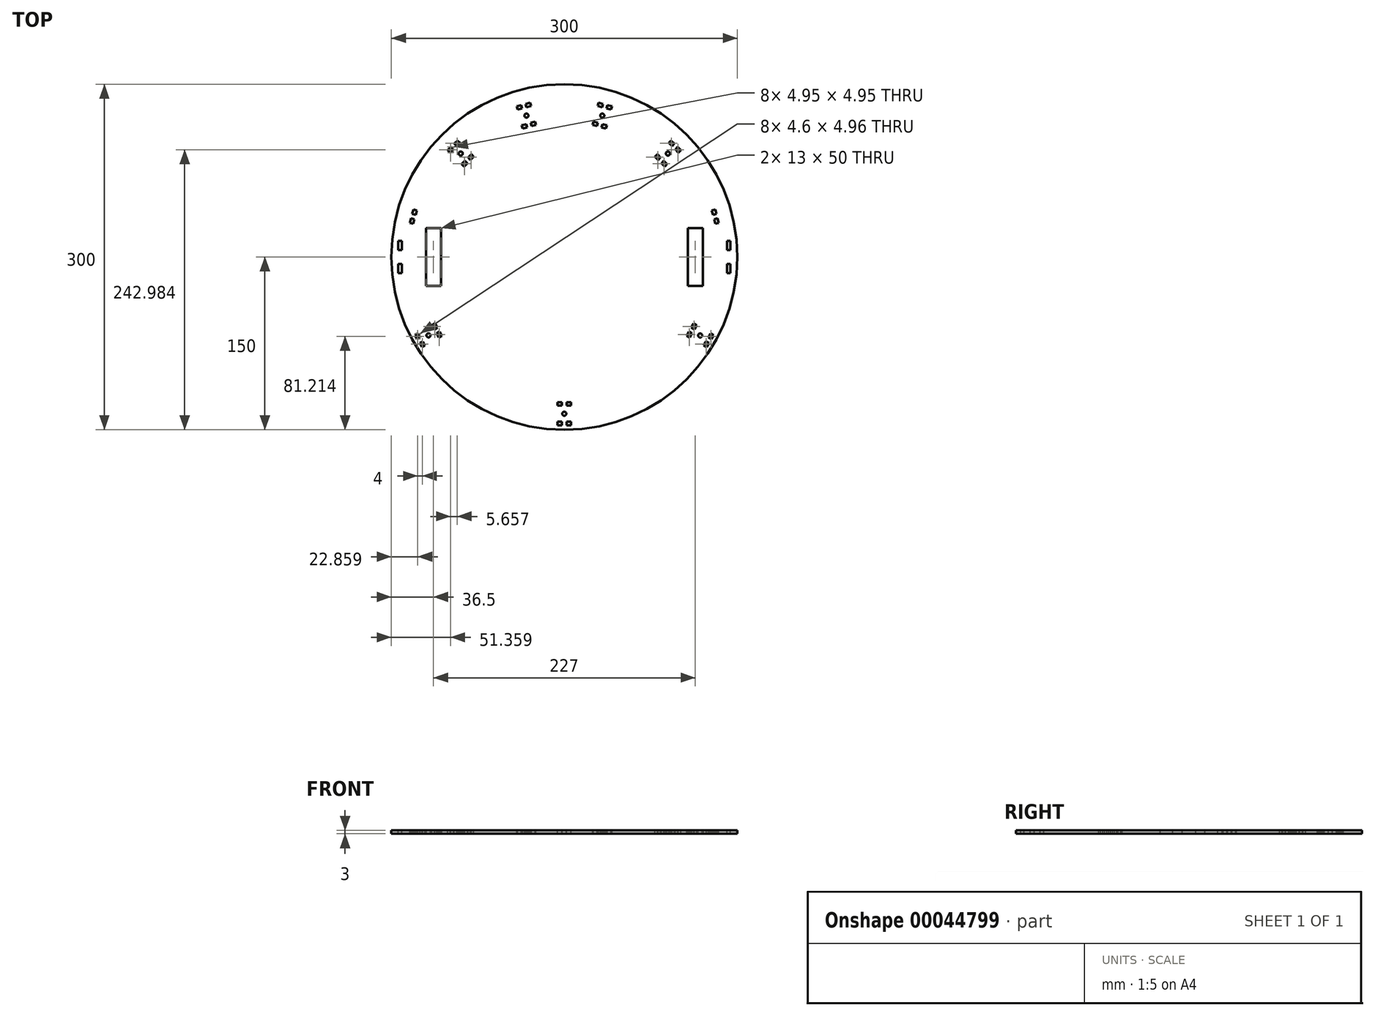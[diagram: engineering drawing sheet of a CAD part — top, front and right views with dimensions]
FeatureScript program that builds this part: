
annotation { "Feature Type Name" : "Feature", "Feature Type Description" : "" }
export const myFeature = defineFeature(function(context is Context, id is Id, definition is map)
    precondition{}
    {
        {
            var Q0;
            Q0=qCreatedBy(makeId("Top.planeOp"),FACE);
            var sketch = newSketch(context, id + "F0", { "sketchPlane" : qUnion([Q0])});
            skCircle(sketch, "E0", {"center": v(0, 0) * mm, "radius": 150 * mm});
            skLineSegment(sketch, "E1", {"start": v(0, 150) * mm, "end": v(0, -150) * mm, "construction": true});
            skLineSegment(sketch, "E2.bottom", {"start": v(-120, 25) * mm, "end": v(-107, 25) * mm});
            skLineSegment(sketch, "E2.top", {"start": v(-120, -25) * mm, "end": v(-107, -25) * mm});
            skLineSegment(sketch, "E2.left", {"start": v(-120, 25) * mm, "end": v(-120, -25) * mm});
            skLineSegment(sketch, "E2.right", {"start": v(-107, 25) * mm, "end": v(-107, -25) * mm});
            skLineSegment(sketch, "E3.bottom", {"start": v(-144, -6) * mm, "end": v(-141, -6) * mm});
            skLineSegment(sketch, "E3.top", {"start": v(-144, -14) * mm, "end": v(-141, -14) * mm});
            skLineSegment(sketch, "E3.left", {"start": v(-144, -6) * mm, "end": v(-144, -14) * mm});
            skLineSegment(sketch, "E3.right", {"start": v(-141, -6) * mm, "end": v(-141, -14) * mm});
            skLineSegment(sketch, "E4", {"start": v(150, 0) * mm, "end": v(-150, 0) * mm, "construction": true});
            skPoint(sketch, "E5", {"position": v(-107, 0) * mm});
            skLineSegment(sketch, "E6.MirrorCS", {"start": v(-144, 14) * mm, "end": v(-141, 14) * mm});
            skLineSegment(sketch, "E7.MirrorCS", {"start": v(-141, 6) * mm, "end": v(-141, 14) * mm});
            skLineSegment(sketch, "E8.MirrorCS", {"start": v(-144, 6) * mm, "end": v(-144, 14) * mm});
            skLineSegment(sketch, "E9.MirrorCS", {"start": v(-144, 6) * mm, "end": v(-141, 6) * mm});
            skLineSegment(sketch, "E10.MirrorCS", {"start": v(144, 6) * mm, "end": v(141, 6) * mm});
            skLineSegment(sketch, "E11.MirrorCS", {"start": v(144, 14) * mm, "end": v(141, 14) * mm});
            skLineSegment(sketch, "E12.MirrorCS", {"start": v(144, -6) * mm, "end": v(141, -6) * mm});
            skLineSegment(sketch, "E13.MirrorCS", {"start": v(144, -14) * mm, "end": v(141, -14) * mm});
            skLineSegment(sketch, "E14.MirrorCS", {"start": v(144, -6) * mm, "end": v(144, -14) * mm});
            skLineSegment(sketch, "E15.MirrorCS", {"start": v(141, -6) * mm, "end": v(141, -14) * mm});
            skLineSegment(sketch, "E16.MirrorCS", {"start": v(144, 6) * mm, "end": v(144, 14) * mm});
            skLineSegment(sketch, "E17.MirrorCS", {"start": v(107, 25) * mm, "end": v(107, -25) * mm});
            skLineSegment(sketch, "E18.MirrorCS", {"start": v(120, 25) * mm, "end": v(120, -25) * mm});
            skLineSegment(sketch, "E19.MirrorCS", {"start": v(120, -25) * mm, "end": v(107, -25) * mm});
            skLineSegment(sketch, "E20.MirrorCS", {"start": v(120, 25) * mm, "end": v(107, 25) * mm});
            skPoint(sketch, "E21.MirrorP", {"position": v(107, 0) * mm});
            skLineSegment(sketch, "E22.MirrorCS", {"start": v(141, 6) * mm, "end": v(141, 14) * mm});
            skSolve(sketch);
        }
        {
            var Q0;
            Q0=makeQuery(id+"F0.imprint","IMPRINT",FACE,{"disambiguationData":[TD([[makeQuery(id+"F0.imprint","IMPRINT",EDGE,{"derivedFrom":sQuery(id+"F0.wireOp",EDGE,"E0")}),1.0]])]});
            extrude(context, id + "F1", {"entities" : qUnion([Q0]), "oppositeDirection" : true, "depth" : 3 * mm});
        }
        {
            var Q0;
            Q0=makeQuery(id+"F1.opExtrude","CAP_FACE",FACE,{"disambiguationData":[OSD([sQuery(id+"F0.wireOp",EDGE,"E0"),sQuery(id+"F0.wireOp",EDGE,"E2.bottom"),sQuery(id+"F0.wireOp",EDGE,"E2.top"),sQuery(id+"F0.wireOp",EDGE,"E2.left"),sQuery(id+"F0.wireOp",EDGE,"E2.right"),sQuery(id+"F0.wireOp",EDGE,"E3.bottom"),sQuery(id+"F0.wireOp",EDGE,"E3.top"),sQuery(id+"F0.wireOp",EDGE,"E3.left"),sQuery(id+"F0.wireOp",EDGE,"E3.right"),sQuery(id+"F0.wireOp",EDGE,"cbf36644-4c9d-44f4-99aa-729f08500aa81.MirrorCS"),sQuery(id+"F0.wireOp",EDGE,"cbf36644-4c9d-44f4-99aa-729f08500aa82.MirrorCS"),sQuery(id+"F0.wireOp",EDGE,"cbf36644-4c9d-44f4-99aa-729f08500aa83.MirrorCS"),sQuery(id+"F0.wireOp",EDGE,"cbf36644-4c9d-44f4-99aa-729f08500aa84.MirrorCS"),sQuery(id+"F0.wireOp",EDGE,"868d1104-2d39-4a06-ab7a-803dcc4c7a7c1.MirrorCS"),sQuery(id+"F0.wireOp",EDGE,"868d1104-2d39-4a06-ab7a-803dcc4c7a7c2.MirrorCS"),sQuery(id+"F0.wireOp",EDGE,"868d1104-2d39-4a06-ab7a-803dcc4c7a7c3.MirrorCS"),sQuery(id+"F0.wireOp",EDGE,"868d1104-2d39-4a06-ab7a-803dcc4c7a7c4.MirrorCS")])],"isStart":true});
            var sketch = newSketch(context, id + "F2", { "sketchPlane" : qUnion([Q0])});
            skCircle(sketch, "E23.0", {"center": v(0, 0) * mm, "radius": 150 * mm, "construction": true});
            skLineSegment(sketch, "E24.1", {"start": v(0, 150) * mm, "end": v(0, -150) * mm, "construction": true});
            skLineSegment(sketch, "E25.2", {"start": v(150, 0) * mm, "end": v(-150, 0) * mm, "construction": true});
            skCircle(sketch, "E26.0", {"center": v(0, 0) * mm, "radius": 151 * mm, "construction": true});
            skCircle(sketch, "E27.0", {"center": v(0, 0) * mm, "radius": 154 * mm, "construction": true});
            skLineSegment(sketch, "E28", {"start": v(0, 150) * mm, "end": v(0, 151) * mm, "construction": true});
            skLineSegment(sketch, "E29", {"start": v(0, 151) * mm, "end": v(0, 154) * mm, "construction": true});
            skLineSegment(sketch, "E30", {"start": v(0, 0) * mm, "end": v(-75, 129.9) * mm, "construction": true});
            skLineSegment(sketch, "E31", {"start": v(-75, 129.9) * mm, "end": v(-75.5, 130.77) * mm, "construction": true});
            skLineSegment(sketch, "E32", {"start": v(-75.5, 130.77) * mm, "end": v(-77, 133.37) * mm, "construction": true});
            skLineSegment(sketch, "E33", {"start": v(0, 0) * mm, "end": v(-150, 0) * mm, "construction": true});
            skLineSegment(sketch, "E34", {"start": v(-150, 0) * mm, "end": v(-151, 0) * mm, "construction": true});
            skLineSegment(sketch, "E35", {"start": v(-151, 0) * mm, "end": v(-154, 0) * mm, "construction": true});
            skLineSegment(sketch, "E36", {"start": v(0, 0) * mm, "end": v(-38.82, 144.89) * mm, "construction": true});
            skLineSegment(sketch, "E37", {"start": v(-38.82, 144.89) * mm, "end": v(-39.08, 145.85) * mm, "construction": true});
            skLineSegment(sketch, "E38", {"start": v(-39.08, 145.85) * mm, "end": v(-39.86, 148.75) * mm, "construction": true});
            skLineSegment(sketch, "E39", {"start": v(-41.25, 130.78) * mm, "end": v(-37.4, 131.81) * mm});
            skLineSegment(sketch, "E40", {"start": v(-37.4, 131.81) * mm, "end": v(-36.61, 128.92) * mm});
            skLineSegment(sketch, "E41", {"start": v(-36.61, 128.92) * mm, "end": v(-40.48, 127.88) * mm});
            skLineSegment(sketch, "E42", {"start": v(-40.48, 127.88) * mm, "end": v(-41.25, 130.78) * mm});
            skLineSegment(sketch, "E43", {"start": v(-33, 115.4) * mm, "end": v(-36.85, 114.36) * mm});
            skLineSegment(sketch, "E44", {"start": v(-36.85, 114.36) * mm, "end": v(-36.08, 111.46) * mm});
            skLineSegment(sketch, "E45", {"start": v(-36.08, 111.46) * mm, "end": v(-32.21, 112.5) * mm});
            skLineSegment(sketch, "E46", {"start": v(-33, 115.4) * mm, "end": v(-32.21, 112.5) * mm});
            skCircle(sketch, "E47", {"center": v(-32.87, 122.67) * mm, "radius": 1.75 * mm});
            skLineSegment(sketch, "E48.MirrorCS", {"start": v(-29.66, 133.88) * mm, "end": v(-33.53, 132.85) * mm});
            skLineSegment(sketch, "E49.MirrorCS", {"start": v(-33.53, 132.85) * mm, "end": v(-32.75, 129.95) * mm});
            skLineSegment(sketch, "E50.MirrorCS", {"start": v(-32.75, 129.95) * mm, "end": v(-28.89, 130.99) * mm});
            skLineSegment(sketch, "E51.MirrorCS", {"start": v(-29.13, 116.43) * mm, "end": v(-25.26, 117.46) * mm});
            skLineSegment(sketch, "E52.MirrorCS", {"start": v(-29.13, 116.43) * mm, "end": v(-28.35, 113.53) * mm});
            skLineSegment(sketch, "E53.MirrorCS", {"start": v(-24.49, 114.57) * mm, "end": v(-28.35, 113.53) * mm});
            skLineSegment(sketch, "E54.MirrorCS", {"start": v(-25.26, 117.46) * mm, "end": v(-24.49, 114.57) * mm});
            skLineSegment(sketch, "E55.MirrorCS", {"start": v(-28.89, 130.99) * mm, "end": v(-29.66, 133.88) * mm});
            skLineSegment(sketch, "E56.anchor1", {"start": v(0, 0) * mm, "end": v(-32.87, 122.67) * mm, "construction": true});
            skLineSegment(sketch, "E57", {"start": v(0, 0) * mm, "end": v(-133.37, -77) * mm, "construction": true});
            skCircle(sketch, "E58", {"center": v(-117.78, -68) * mm, "radius": 1.75 * mm});
            skLineSegment(sketch, "E59", {"start": v(-110.72, -66.23) * mm, "end": v(-108.72, -69.7) * mm});
            skLineSegment(sketch, "E60", {"start": v(-122.84, -73.23) * mm, "end": v(-120.84, -76.7) * mm});
            skLineSegment(sketch, "E61", {"start": v(-125.44, -74.73) * mm, "end": v(-122.84, -73.23) * mm});
            skLineSegment(sketch, "E62", {"start": v(-110.72, -66.23) * mm, "end": v(-108.12, -64.73) * mm});
            skLineSegment(sketch, "E63", {"start": v(-106.12, -68.2) * mm, "end": v(-108.12, -64.73) * mm});
            skLineSegment(sketch, "E64", {"start": v(-123.44, -78.2) * mm, "end": v(-125.44, -74.73) * mm});
            skLineSegment(sketch, "E65", {"start": v(-108.72, -69.7) * mm, "end": v(-106.12, -68.2) * mm});
            skLineSegment(sketch, "E66", {"start": v(-120.84, -76.7) * mm, "end": v(-123.44, -78.2) * mm});
            skPoint(sketch, "E67", {"position": v(-130.77, -75.5) * mm});
            skLineSegment(sketch, "E68.MirrorCS", {"start": v(-112.72, -62.77) * mm, "end": v(-110.12, -61.27) * mm});
            skLineSegment(sketch, "E69.MirrorCS", {"start": v(-112.12, -57.8) * mm, "end": v(-110.12, -61.27) * mm});
            skLineSegment(sketch, "E70.MirrorCS", {"start": v(-114.72, -59.3) * mm, "end": v(-112.12, -57.8) * mm});
            skLineSegment(sketch, "E71.MirrorCS", {"start": v(-112.72, -62.77) * mm, "end": v(-114.72, -59.3) * mm});
            skLineSegment(sketch, "E72.MirrorCS", {"start": v(-124.84, -69.77) * mm, "end": v(-126.84, -66.3) * mm});
            skLineSegment(sketch, "E73.MirrorCS", {"start": v(-126.84, -66.3) * mm, "end": v(-129.44, -67.8) * mm});
            skLineSegment(sketch, "E74.MirrorCS", {"start": v(-127.44, -71.27) * mm, "end": v(-124.84, -69.77) * mm});
            skLineSegment(sketch, "E75.MirrorCS", {"start": v(-129.44, -67.8) * mm, "end": v(-127.44, -71.27) * mm});
            skLineSegment(sketch, "E76.MirrorCS", {"start": v(110.72, -66.23) * mm, "end": v(108.12, -64.73) * mm});
            skLineSegment(sketch, "E77.MirrorCS", {"start": v(110.72, -66.23) * mm, "end": v(108.72, -69.7) * mm});
            skLineSegment(sketch, "E78.MirrorCS", {"start": v(129.44, -67.8) * mm, "end": v(127.44, -71.27) * mm});
            skLineSegment(sketch, "E79.MirrorCS", {"start": v(127.44, -71.27) * mm, "end": v(124.84, -69.77) * mm});
            skLineSegment(sketch, "E80.MirrorCS", {"start": v(114.72, -59.3) * mm, "end": v(112.12, -57.8) * mm});
            skLineSegment(sketch, "E81.MirrorCS", {"start": v(112.12, -57.8) * mm, "end": v(110.12, -61.27) * mm});
            skLineSegment(sketch, "E82.MirrorCS", {"start": v(112.72, -62.77) * mm, "end": v(110.12, -61.27) * mm});
            skLineSegment(sketch, "E83.MirrorCS", {"start": v(112.72, -62.77) * mm, "end": v(114.72, -59.3) * mm});
            skLineSegment(sketch, "E84.MirrorCS", {"start": v(124.84, -69.77) * mm, "end": v(126.84, -66.3) * mm});
            skLineSegment(sketch, "E85.MirrorCS", {"start": v(126.84, -66.3) * mm, "end": v(129.44, -67.8) * mm});
            skLineSegment(sketch, "E86.MirrorCS", {"start": v(106.12, -68.2) * mm, "end": v(108.12, -64.73) * mm});
            skLineSegment(sketch, "E87.MirrorCS", {"start": v(108.72, -69.7) * mm, "end": v(106.12, -68.2) * mm});
            skCircle(sketch, "E88.MirrorC", {"center": v(117.78, -68) * mm, "radius": 1.75 * mm});
            skLineSegment(sketch, "E89.MirrorCS", {"start": v(125.44, -74.73) * mm, "end": v(122.84, -73.23) * mm});
            skLineSegment(sketch, "E90.MirrorCS", {"start": v(122.84, -73.23) * mm, "end": v(120.84, -76.7) * mm});
            skLineSegment(sketch, "E91.MirrorCS", {"start": v(123.44, -78.2) * mm, "end": v(125.44, -74.73) * mm});
            skLineSegment(sketch, "E92.MirrorCS", {"start": v(120.84, -76.7) * mm, "end": v(123.44, -78.2) * mm});
            skPoint(sketch, "E93.MirrorP", {"position": v(130.77, -75.5) * mm});
            skPoint(sketch, "E94.1.0", {"position": v(0, -151) * mm});
            skCircle(sketch, "E94.1.1", {"center": v(0, -136) * mm, "radius": 1.75 * mm});
            skPoint(sketch, "E94.1.2", {"position": v(0, -151) * mm});
            skLineSegment(sketch, "E94.1.3", {"start": v(6, -129) * mm, "end": v(6, -126) * mm});
            skLineSegment(sketch, "E94.1.4", {"start": v(-2, -129) * mm, "end": v(-2, -126) * mm});
            skLineSegment(sketch, "E94.1.5", {"start": v(6, -143) * mm, "end": v(6, -146) * mm});
            skLineSegment(sketch, "E94.1.6", {"start": v(-6, -129) * mm, "end": v(-6, -126) * mm});
            skLineSegment(sketch, "E94.1.7", {"start": v(-2, -143) * mm, "end": v(-6, -143) * mm});
            skLineSegment(sketch, "E94.1.8", {"start": v(-6, -143) * mm, "end": v(-6, -146) * mm});
            skLineSegment(sketch, "E94.1.9", {"start": v(-2, -146) * mm, "end": v(-2, -143) * mm});
            skLineSegment(sketch, "E94.1.10", {"start": v(6, -146) * mm, "end": v(2, -146) * mm});
            skLineSegment(sketch, "E94.1.11", {"start": v(2, -143) * mm, "end": v(6, -143) * mm});
            skLineSegment(sketch, "E94.1.12", {"start": v(2, -146) * mm, "end": v(2, -143) * mm});
            skLineSegment(sketch, "E94.1.13", {"start": v(-6, -146) * mm, "end": v(-2, -146) * mm});
            skLineSegment(sketch, "E94.1.14", {"start": v(2, -129) * mm, "end": v(6, -129) * mm});
            skLineSegment(sketch, "E94.1.15", {"start": v(6, -126) * mm, "end": v(2, -126) * mm});
            skLineSegment(sketch, "E94.1.16", {"start": v(2, -129) * mm, "end": v(2, -126) * mm});
            skLineSegment(sketch, "E94.1.17", {"start": v(-2, -129) * mm, "end": v(-6, -129) * mm});
            skLineSegment(sketch, "E94.1.18", {"start": v(-6, -126) * mm, "end": v(-2, -126) * mm});
            skLineSegment(sketch, "E94.anchor1", {"start": v(0, 0) * mm, "end": v(-130.77, -75.5) * mm, "construction": true});
            skLineSegment(sketch, "E94.anchor2", {"start": v(0, 0) * mm, "end": v(0, -151) * mm, "construction": true});
            skLineSegment(sketch, "E95.1.0", {"start": v(-86.97, 78.49) * mm, "end": v(-84.15, 81.32) * mm});
            skLineSegment(sketch, "E95.1.1", {"start": v(-89.1, 80.61) * mm, "end": v(-86.97, 78.49) * mm});
            skLineSegment(sketch, "E95.1.2", {"start": v(-86.27, 83.44) * mm, "end": v(-84.15, 81.32) * mm});
            skLineSegment(sketch, "E95.1.3", {"start": v(-83.44, 86.27) * mm, "end": v(-81.32, 84.15) * mm});
            skLineSegment(sketch, "E95.1.4", {"start": v(-78.49, 86.97) * mm, "end": v(-81.32, 84.15) * mm});
            skLineSegment(sketch, "E95.1.5", {"start": v(-86.27, 83.44) * mm, "end": v(-89.1, 80.61) * mm});
            skLineSegment(sketch, "E95.1.6", {"start": v(-80.61, 89.1) * mm, "end": v(-78.49, 86.97) * mm});
            skLineSegment(sketch, "E95.1.7", {"start": v(-83.44, 86.27) * mm, "end": v(-80.61, 89.1) * mm});
            skCircle(sketch, "E95.1.8", {"center": v(-89.8, 89.8) * mm, "radius": 1.75 * mm});
            skLineSegment(sketch, "E95.1.9", {"start": v(-99, 90.5) * mm, "end": v(-101.12, 92.63) * mm});
            skLineSegment(sketch, "E95.1.10", {"start": v(-96.17, 93.34) * mm, "end": v(-99, 90.5) * mm});
            skLineSegment(sketch, "E95.1.11", {"start": v(-98.29, 95.46) * mm, "end": v(-96.17, 93.34) * mm});
            skLineSegment(sketch, "E95.1.12", {"start": v(-93.34, 96.17) * mm, "end": v(-90.5, 99) * mm});
            skLineSegment(sketch, "E95.1.13", {"start": v(-101.12, 92.63) * mm, "end": v(-98.29, 95.46) * mm});
            skLineSegment(sketch, "E95.1.14", {"start": v(-95.46, 98.29) * mm, "end": v(-93.34, 96.17) * mm});
            skLineSegment(sketch, "E95.1.15", {"start": v(-90.5, 99) * mm, "end": v(-92.63, 101.12) * mm});
            skLineSegment(sketch, "E95.1.16", {"start": v(-92.63, 101.12) * mm, "end": v(-95.46, 98.29) * mm});
            skLineSegment(sketch, "E95.1.17", {"start": v(-106.07, 106.07) * mm, "end": v(-106.77, 106.77) * mm, "construction": true});
            skLineSegment(sketch, "E95.1.18", {"start": v(-106.77, 106.77) * mm, "end": v(-108.9, 108.9) * mm, "construction": true});
            skLineSegment(sketch, "E95.1.19", {"start": v(0, 0) * mm, "end": v(-106.07, 106.07) * mm, "construction": true});
            skLineSegment(sketch, "E95.anchor2", {"start": v(0, 0) * mm, "end": v(-89.8, 89.8) * mm, "construction": true});
            skLineSegment(sketch, "E96.1.0", {"start": v(-130.99, 28.89) * mm, "end": v(-133.88, 29.66) * mm});
            skLineSegment(sketch, "E96.1.1", {"start": v(-129.95, 32.75) * mm, "end": v(-130.99, 28.89) * mm});
            skLineSegment(sketch, "E96.1.2", {"start": v(-133.88, 29.66) * mm, "end": v(-132.85, 33.53) * mm});
            skLineSegment(sketch, "E96.1.3", {"start": v(-132.85, 33.53) * mm, "end": v(-129.95, 32.75) * mm});
            skLineSegment(sketch, "E96.1.4", {"start": v(-131.81, 37.4) * mm, "end": v(-128.92, 36.61) * mm});
            skLineSegment(sketch, "E96.1.5", {"start": v(-128.92, 36.61) * mm, "end": v(-127.88, 40.48) * mm});
            skLineSegment(sketch, "E96.1.6", {"start": v(-130.78, 41.25) * mm, "end": v(-131.81, 37.4) * mm});
            skLineSegment(sketch, "E96.1.7", {"start": v(-127.88, 40.48) * mm, "end": v(-130.78, 41.25) * mm});
            skLineSegment(sketch, "E96.1.8", {"start": v(0, 0) * mm, "end": v(-122.67, 32.87) * mm, "construction": true});
            skLineSegment(sketch, "E96.1.9", {"start": v(0, 0) * mm, "end": v(-144.89, 38.82) * mm, "construction": true});
            skLineSegment(sketch, "E96.1.10", {"start": v(-145.85, 39.08) * mm, "end": v(-148.75, 39.86) * mm, "construction": true});
            skLineSegment(sketch, "E96.1.11", {"start": v(-144.89, 38.82) * mm, "end": v(-145.85, 39.08) * mm, "construction": true});
            skLineSegment(sketch, "E96.anchor2", {"start": v(0, 0) * mm, "end": v(-122.67, 32.87) * mm, "construction": true});
            skLineSegment(sketch, "E97.MirrorCS", {"start": v(29.66, 133.88) * mm, "end": v(33.53, 132.85) * mm});
            skLineSegment(sketch, "E98.MirrorCS", {"start": v(28.89, 130.99) * mm, "end": v(29.66, 133.88) * mm});
            skLineSegment(sketch, "E99.MirrorCS", {"start": v(41.25, 130.78) * mm, "end": v(37.4, 131.81) * mm});
            skLineSegment(sketch, "E100.MirrorCS", {"start": v(33.53, 132.85) * mm, "end": v(32.75, 129.95) * mm});
            skLineSegment(sketch, "E101.MirrorCS", {"start": v(32.75, 129.95) * mm, "end": v(28.89, 130.99) * mm});
            skLineSegment(sketch, "E102.MirrorCS", {"start": v(37.4, 131.81) * mm, "end": v(36.61, 128.92) * mm});
            skLineSegment(sketch, "E103.MirrorCS", {"start": v(36.61, 128.92) * mm, "end": v(40.48, 127.88) * mm});
            skLineSegment(sketch, "E104.MirrorCS", {"start": v(40.48, 127.88) * mm, "end": v(41.25, 130.78) * mm});
            skLineSegment(sketch, "E105.MirrorCS", {"start": v(29.13, 116.43) * mm, "end": v(25.26, 117.46) * mm});
            skLineSegment(sketch, "E106.MirrorCS", {"start": v(25.26, 117.46) * mm, "end": v(24.49, 114.57) * mm});
            skLineSegment(sketch, "E107.MirrorCS", {"start": v(33, 115.4) * mm, "end": v(36.85, 114.36) * mm});
            skLineSegment(sketch, "E108.MirrorCS", {"start": v(29.13, 116.43) * mm, "end": v(28.35, 113.53) * mm});
            skLineSegment(sketch, "E109.MirrorCS", {"start": v(33, 115.4) * mm, "end": v(32.21, 112.5) * mm});
            skLineSegment(sketch, "E110.MirrorCS", {"start": v(36.85, 114.36) * mm, "end": v(36.08, 111.46) * mm});
            skCircle(sketch, "E111.MirrorC", {"center": v(32.87, 122.67) * mm, "radius": 1.75 * mm});
            skLineSegment(sketch, "E112.MirrorCS", {"start": v(24.49, 114.57) * mm, "end": v(28.35, 113.53) * mm});
            skLineSegment(sketch, "E113.MirrorCS", {"start": v(36.08, 111.46) * mm, "end": v(32.21, 112.5) * mm});
            skLineSegment(sketch, "E114.MirrorCS", {"start": v(95.46, 98.29) * mm, "end": v(93.34, 96.17) * mm});
            skLineSegment(sketch, "E115.MirrorCS", {"start": v(98.29, 95.46) * mm, "end": v(96.17, 93.34) * mm});
            skLineSegment(sketch, "E116.MirrorCS", {"start": v(101.12, 92.63) * mm, "end": v(98.29, 95.46) * mm});
            skLineSegment(sketch, "E117.MirrorCS", {"start": v(99, 90.5) * mm, "end": v(101.12, 92.63) * mm});
            skLineSegment(sketch, "E118.MirrorCS", {"start": v(80.61, 89.1) * mm, "end": v(78.49, 86.97) * mm});
            skLineSegment(sketch, "E119.MirrorCS", {"start": v(78.49, 86.97) * mm, "end": v(81.32, 84.15) * mm});
            skLineSegment(sketch, "E120.MirrorCS", {"start": v(83.44, 86.27) * mm, "end": v(81.32, 84.15) * mm});
            skLineSegment(sketch, "E121.MirrorCS", {"start": v(86.27, 83.44) * mm, "end": v(84.15, 81.32) * mm});
            skLineSegment(sketch, "E122.MirrorCS", {"start": v(86.27, 83.44) * mm, "end": v(89.1, 80.61) * mm});
            skLineSegment(sketch, "E123.MirrorCS", {"start": v(86.97, 78.49) * mm, "end": v(84.15, 81.32) * mm});
            skLineSegment(sketch, "E124.MirrorCS", {"start": v(89.1, 80.61) * mm, "end": v(86.97, 78.49) * mm});
            skLineSegment(sketch, "E125.MirrorCS", {"start": v(93.34, 96.17) * mm, "end": v(90.5, 99) * mm});
            skLineSegment(sketch, "E126.MirrorCS", {"start": v(96.17, 93.34) * mm, "end": v(99, 90.5) * mm});
            skCircle(sketch, "E127.MirrorC", {"center": v(89.8, 89.8) * mm, "radius": 1.75 * mm});
            skLineSegment(sketch, "E128.MirrorCS", {"start": v(83.44, 86.27) * mm, "end": v(80.61, 89.1) * mm});
            skLineSegment(sketch, "E129.MirrorCS", {"start": v(90.5, 99) * mm, "end": v(92.63, 101.12) * mm});
            skLineSegment(sketch, "E130.MirrorCS", {"start": v(92.63, 101.12) * mm, "end": v(95.46, 98.29) * mm});
            skLineSegment(sketch, "E131.MirrorCS", {"start": v(127.88, 40.48) * mm, "end": v(130.78, 41.25) * mm});
            skLineSegment(sketch, "E132.MirrorCS", {"start": v(128.92, 36.61) * mm, "end": v(127.88, 40.48) * mm});
            skLineSegment(sketch, "E133.MirrorCS", {"start": v(131.81, 37.4) * mm, "end": v(128.92, 36.61) * mm});
            skLineSegment(sketch, "E134.MirrorCS", {"start": v(132.85, 33.53) * mm, "end": v(129.95, 32.75) * mm});
            skLineSegment(sketch, "E135.MirrorCS", {"start": v(129.95, 32.75) * mm, "end": v(130.99, 28.89) * mm});
            skLineSegment(sketch, "E136.MirrorCS", {"start": v(130.99, 28.89) * mm, "end": v(133.88, 29.66) * mm});
            skLineSegment(sketch, "E137.MirrorCS", {"start": v(130.78, 41.25) * mm, "end": v(131.81, 37.4) * mm});
            skLineSegment(sketch, "E138.MirrorCS", {"start": v(133.88, 29.66) * mm, "end": v(132.85, 33.53) * mm});
            skSolve(sketch);
        }
        {
            var Q0;
            Q0=qSketchRegion(id+"F2",true);
            extrude(context, id + "F3", {"entities" : qUnion([Q0]), "operationType" : NewBodyOperationType.REMOVE, "endBound" : BoundingType.UP_TO_NEXT, "oppositeDirection" : true, "depth" : 25 * mm});
        }
    });
